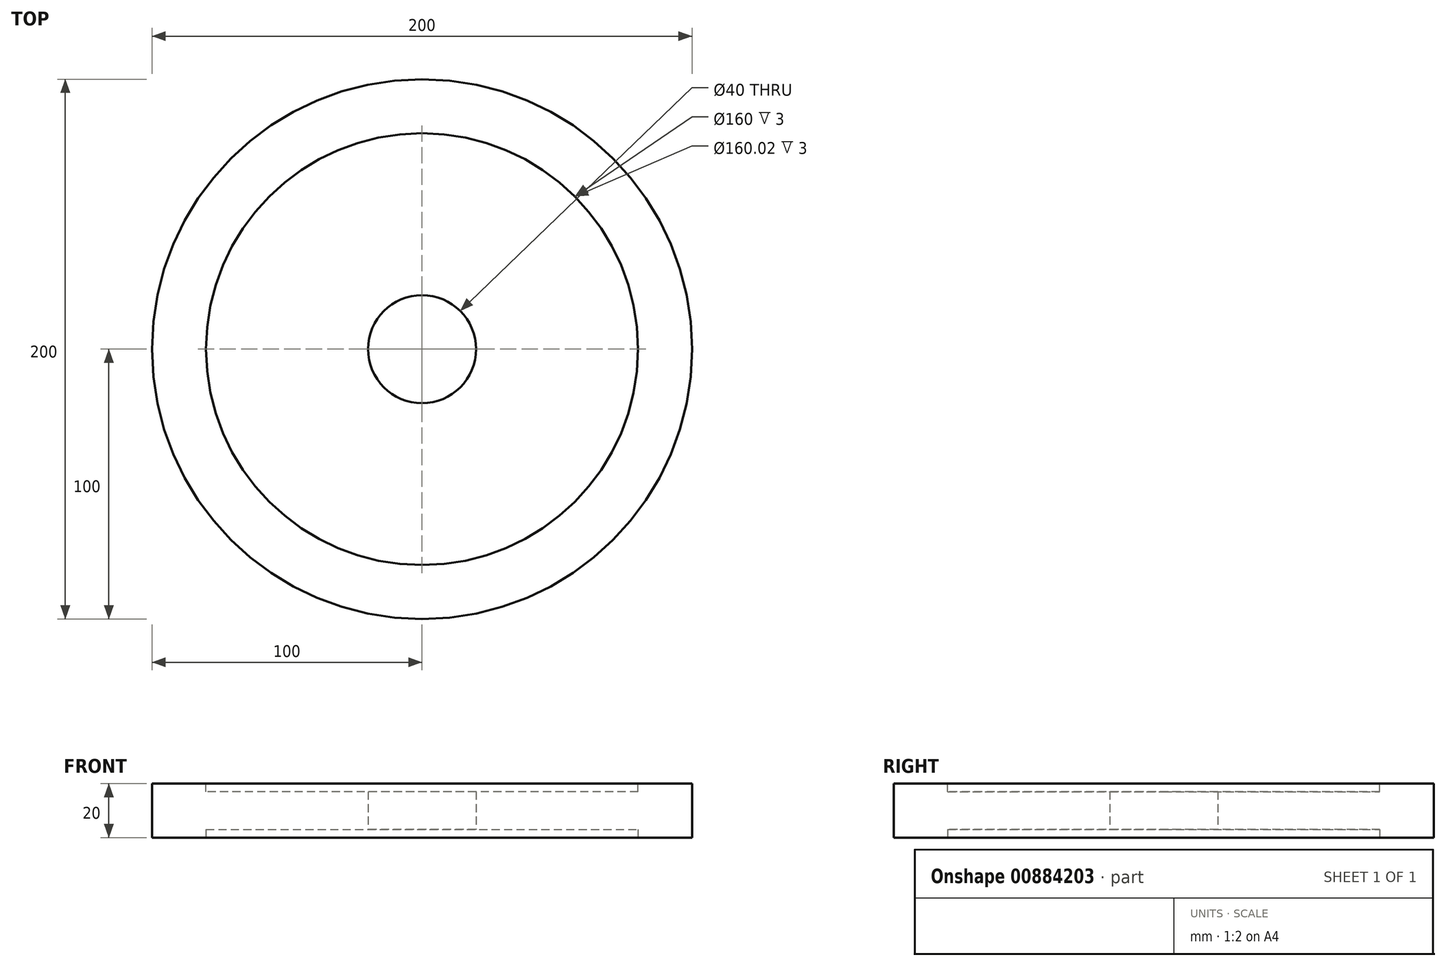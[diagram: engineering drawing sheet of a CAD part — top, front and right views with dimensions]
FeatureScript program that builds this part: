
annotation { "Feature Type Name" : "Feature", "Feature Type Description" : "" }
export const myFeature = defineFeature(function(context is Context, id is Id, definition is map)
    precondition{}
    {
        {
            var Q0;
            Q0=qCreatedBy(makeId("Top.planeOp"),FACE);
            var sketch = newSketch(context, id + "F0", { "sketchPlane" : qUnion([Q0])});
            skCircle(sketch, "E0", {"center": v(0, 0) * mm, "radius": 100 * mm});
            skCircle(sketch, "E1", {"center": v(0, 0) * mm, "radius": 80 * mm});
            skCircle(sketch, "E2", {"center": v(0, 0) * mm, "radius": 20 * mm});
            skCircle(sketch, "E3", {"center": v(0, 0) * mm, "radius": 95 * mm});
            skSolve(sketch);
        }
        {
            var Q0;
            Q0=makeQuery(id+"F0.imprint","IMPRINT",FACE,{"disambiguationData":[TD([[makeQuery(id+"F0.imprint","IMPRINT",EDGE,{"derivedFrom":sQuery(id+"F0.wireOp",EDGE,"E0")}),1.0]])]});
            var Q1;
            Q1=makeQuery(id+"F0.imprint","IMPRINT",FACE,{"disambiguationData":[TD([[makeQuery(id+"F0.imprint","IMPRINT",EDGE,{"derivedFrom":sQuery(id+"F0.wireOp",EDGE,"E1")}),1.0]])]});
            var Q2;
            Q2=makeQuery(id+"F0.imprint","IMPRINT",FACE,{"disambiguationData":[TD([[makeQuery(id+"F0.imprint","IMPRINT",EDGE,{"derivedFrom":sQuery(id+"F0.wireOp",EDGE,"E1")}),-1.0]])]});
            extrude(context, id + "F1", {"entities" : qUnion([Q0, Q1, Q2]), "depth" : 20 * mm, "offsetDistance" : 25.4 * mm});
        }
        {
            var Q0;
            Q0=makeQuery(id+"F1.opExtrude","CAP_FACE",FACE,{"disambiguationData":[OSD([sQuery(id+"F0.wireOp",EDGE,"E0"),sQuery(id+"F0.wireOp",EDGE,"E2")])],"isStart":false});
            var sketch = newSketch(context, id + "F2", { "sketchPlane" : qUnion([Q0])});
            skCircle(sketch, "E4", {"center": v(0, 0) * mm, "radius": 80 * mm});
            skSolve(sketch);
        }
        {
            var Q0;
            Q0=makeQuery(id+"F2.imprint","IMPRINT",FACE,{"disambiguationData":[TD([[makeQuery(id+"F2.imprint","IMPRINT",EDGE,{"derivedFrom":sQuery(id+"F2.wireOp",EDGE,"E4")}),1.0]])]});
            extrude(context, id + "F3", {"entities" : qUnion([Q0]), "operationType" : NewBodyOperationType.REMOVE, "oppositeDirection" : true, "depth" : 3 * mm, "offsetDistance" : 25.4 * mm});
        }
        {
            var Q0;
            Q0=makeQuery(id+"F1.opExtrude","CAP_FACE",FACE,{"disambiguationData":[OSD([sQuery(id+"F0.wireOp",EDGE,"E0"),sQuery(id+"F0.wireOp",EDGE,"E2")])],"isStart":true});
            var sketch = newSketch(context, id + "F4", { "sketchPlane" : qUnion([Q0])});
            skCircle(sketch, "E5", {"center": v(0, 0) * mm, "radius": 80.01 * mm});
            skSolve(sketch);
        }
        {
            var Q0;
            Q0=makeQuery(id+"F4.imprint","IMPRINT",FACE,{"disambiguationData":[TD([[makeQuery(id+"F4.imprint","IMPRINT",EDGE,{"derivedFrom":sQuery(id+"F4.wireOp",EDGE,"E5")}),1.0]])]});
            extrude(context, id + "F5", {"entities" : qUnion([Q0]), "operationType" : NewBodyOperationType.REMOVE, "oppositeDirection" : true, "depth" : 3 * mm, "offsetDistance" : 25.4 * mm});
        }
    });
